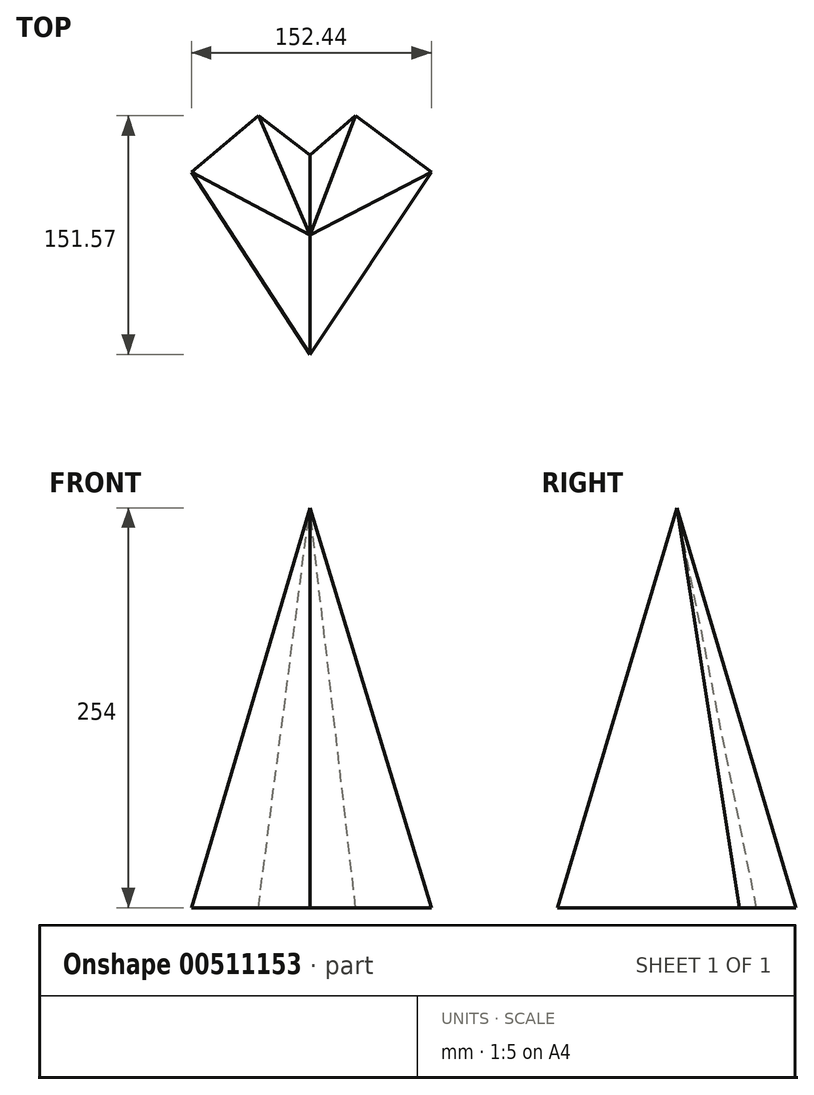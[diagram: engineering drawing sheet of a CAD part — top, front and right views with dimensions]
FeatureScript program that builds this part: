
annotation { "Feature Type Name" : "Feature", "Feature Type Description" : "" }
export const myFeature = defineFeature(function(context is Context, id is Id, definition is map)
    precondition{}
    {
        {
            var Q0;
            Q0=qCreatedBy(makeId("Top.planeOp"),FACE);
            var sketch = newSketch(context, id + "F0", { "sketchPlane" : qUnion([Q0])});
            skLineSegment(sketch, "E0", {"start": v(0, 50.57) * mm, "end": v(-32.65, 75.64) * mm});
            skLineSegment(sketch, "E1", {"start": v(-32.65, 75.64) * mm, "end": v(-75.2, 39.79) * mm});
            skLineSegment(sketch, "E2", {"start": v(-75.2, 39.79) * mm, "end": v(0, -75.93) * mm});
            skLineSegment(sketch, "E3", {"start": v(0, -75.93) * mm, "end": v(77.24, 39.79) * mm});
            skLineSegment(sketch, "E4", {"start": v(77.24, 39.79) * mm, "end": v(29.15, 75.64) * mm});
            skLineSegment(sketch, "E5", {"start": v(29.15, 75.64) * mm, "end": v(0, 50.57) * mm});
            skSolve(sketch);
        }
        {
            var Q0;
            Q0=qCreatedBy(makeId("Top.planeOp"),FACE);
            cPlane(context, id + "F1", {"entities" : qUnion([Q0]), "cplaneType" : CPlaneType.OFFSET, "offset" : 254 * mm, "width" : 152.4 * mm, "height" : 152.4 * mm});
        }
        {
            var Q0;
            Q0=qCreatedBy(id+"F1.planeOp",FACE);
            var sketch = newSketch(context, id + "F2", { "sketchPlane" : qUnion([Q0])});
            skPoint(sketch, "E6", {"position": v(0, 0) * mm});
            skSolve(sketch);
        }
        {
            var Q0;
            Q0=makeQuery(id+"F0.imprint","IMPRINT",FACE,{"disambiguationData":[TD([[makeQuery(id+"F0.imprint","IMPRINT",EDGE,{"derivedFrom":sQuery(id+"F0.wireOp",EDGE,"E0")}),1.0]])]});
            var Q1;
            Q1=sQuery(id+"F2.wireOp",VERTEX,"E6");
            loft(context, id + "F3", {"sheetProfilesArray" : [{ "sheetProfileEntities" : qUnion([Q0]) }, { "sheetProfileEntities" : qUnion([Q1]) }]});
        }
    });
